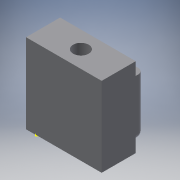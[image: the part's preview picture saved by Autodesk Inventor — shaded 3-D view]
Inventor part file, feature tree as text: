
AUTODESK INVENTOR PART (.ipt)
format: ipt  version: 2018 (Build 220112000, 112)  size: 646,656 bytes
history: native  units: in
note: dims shown in document units (in); Inventor stores cm internally (conversion verified against a paired STEP export)
features: extrude x23, sketch x23, projected_geometry x7, fillet x6, other x6, plane x4, reference x4
ambient origin geometry x8: Origin, YZ Plane, XZ Plane, XY Plane, X Axis, Y Axis, Z Axis, Center Point
bodies: Body1 (feature_tree)
feature tree (73):
  extrude  "Extrusion2"  Depth=0.435in
  sketch  "Sketch3"  dims[d6=0.385in d7=0.0in d9=0.092in]
  extrude  "Extrusion6"  Depth=0.092in
  extrude  "Extrusion7"  Depth=0.1in
  extrude  "Extrusion8"  Depth=0.5814in
  extrude  "Extrusion9"  Depth=0.3937in
  extrude  "Extrusion10"  Depth=0.05in
  extrude  "Extrusion11"  Depth=0.15in
  extrude  "Extrusion12"  Depth=0.4in
  extrude  "Extrusion13"  Depth=0.385in TaperAngle=0.0deg
  extrude  "Extrusion14"  Depth=2.5in
  extrude  "Extrusion15"  Depth=0.25in
  extrude  "Extrusion16"  Depth=0.0394in TaperAngle=0.0deg
  extrude  "Extrusion17"  Depth=0.0984in
  extrude  "Extrusion18"  Depth=0.0394in TaperAngle=0.0deg
  extrude  "Extrusion19"  Depth=0.0472in TaperAngle=0.0deg
  fillet  "Fillet2"  Radius=0.1177in
  extrude  "Extrusion20"  Depth=0.3937in
  extrude  "Extrusion21"  Depth=0.3937in TaperAngle=0.0deg
  sketch  "Sketch21"  dims[d114=0.3937in d115=0.0787in d116=0.0in]
  plane  "Work Plane1"
  plane  "Work Plane2"
  extrude  "Extrusion23"  Depth=0.0394in
  sketch  "Sketch22"  dims[d117=1.0in d118=0.0in d119=0.0394in]
  sketch  "Sketch23"  dims[d120=1.0in d121=0.5in d122=0.0in d123=0.0in d124=0.2362in d125=0.0in]
  plane  "Work Plane3"
  extrude  "Extrusion24"  Depth=0.2362in TaperAngle=0.0deg
  extrude  "Extrusion25"  Depth=0.0394in TaperAngle=0.0deg
  fillet  "Fillet5"  Radius=0.1575in
  fillet  "Fillet6"  Radius=0.0394in
  plane  "Work Plane4"
  extrude  "Extrusion28"  Depth=0.0394in
  extrude  "Extrusion29"  Depth=0.3937in TaperAngle=0.0deg
  extrude  "Extrusion30"  Depth=0.0197in TaperAngle=0.0deg
  fillet  "Fillet11"  Radius=0.315in
  fillet  "Fillet12"  Radius=0.0197in
  fillet  "Fillet13"  Radius=0.0197in
  sketch  "Sketch2"  dims[d4=2.5in d5=0.435in]
  sketch  "Sketch5"  dims[d58=0.1in d59=0.0in d60=0.1in]
  projected_geometry  "Projected Loop1"
  projected_geometry  "Projected Loop2"
  projected_geometry  "Projected Loop3"
  sketch  "Sketch7"  dims[d61=0.385in d62=0.0in d63=0.5814in]
  sketch  "Sketch8"  dims[d64=0.5814in d72=7.874in d74=0.1271in d75=0.3937in d77=1.0in]
  sketch  "Sketch9"  dims[d79=0.25in d80=0.0in d81=0.05in]
  sketch  "Sketch10"  dims[d82=0.385in d83=0.0in d84=0.15in]
  sketch  "Sketch11"  dims[d85=0.05in d86=0.4in]
  projected_geometry  "Projected Loop5"
  sketch  "Sketch12"  dims[d87=0.385in d88=0.0in d89=0.385in d90=0.0in]
  projected_geometry  "Projected Loop6"
  sketch  "Sketch13"  dims[d91=1.0in d92=0.0in d93=2.5in]
  sketch  "Sketch14"  dims[d95=0.1378in d96=0.0in d97=0.25in]
  sketch  "Sketch15"  dims[d98=0.25in d99=0.0394in d100=0.0in]
  sketch  "Sketch16"  dims[d101=0.0984in d102=0.0984in]
  reference  "Reference1"
  sketch  "Sketch17"  dims[d103=0.0394in d104=0.0in d106=1.0in d107=0.0in]
  reference  "Reference2"
  sketch  "Sketch18"  dims[d108=0.0591in d109=0.0472in d110=0.0in d111=0.1177in]
  projected_geometry  "Projected Loop7"
  sketch  "Sketch19"  dims[d112=0.1177in d113=0.3937in]
  sketch  "Sketch24"  dims[d129=100.0in d130=0.0in d131=100.0in d132=0.0in d133=0.1575in d134=0.0in d141=0.0394in]
  projected_geometry  "Projected Loop8"
  sketch  "Sketch27"  dims[d142=0.0394in d145=0.115in]
  sketch  "Sketch28"  dims[d146=0.1083in d147=0.3937in d148=0.0in]
  reference  "Reference3"
  sketch  "Sketch29"  dims[d153=0.2756in d154=0.315in d155=0.0in d156=0.315in d157=0.0in d158=0.0197in d159=0.0197in d160=0.0197in]
  reference  "Reference4"
  other  "<userpath>\OneDrive\Documents\Inventor\TSA\2018\Animatronics\Tortoise\TurtleAssembly2.iam"
  other  "TurtleAssembly2.iam"
  other  "SyringEnd:5"
  other  "SyringEnd:4"
  other  "Glyptodon.iam"
  other  "Tail3:1"
